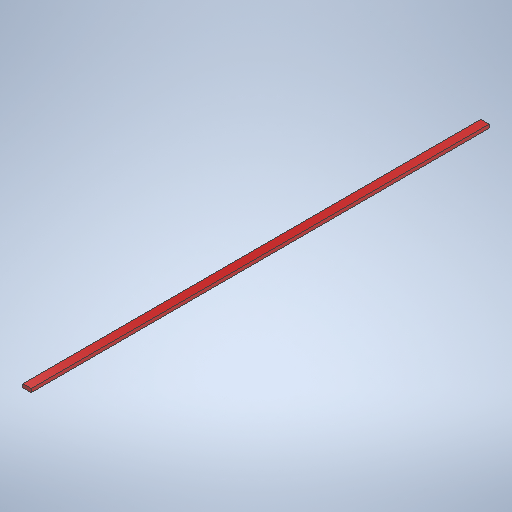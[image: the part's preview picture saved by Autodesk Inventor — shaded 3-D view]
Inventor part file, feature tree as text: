
AUTODESK INVENTOR PART (.ipt)
format: ipt  version: 2025.1 (Build 291241020, 241B)  size: 254,464 bytes
history: native  units: in
note: dims shown in document units (in); Inventor stores cm internally (conversion verified against a paired STEP export)
features: extrude x1, sketch x1, other x1
ambient origin geometry x8: Origin, YZ Plane, XZ Plane, XY Plane, X Axis, Y Axis, Z Axis, Center Point
bodies: Solid1 (feature_tree)
feature tree (3):
  extrude  "Extrusion1"  Depth=1.5in
  sketch  "Sketch1"  dims[d0=3.5in d1=1.5in d2=192.0in d3=96.0in d4=0.0in d5=0.0in]
  other  "Finish1"
